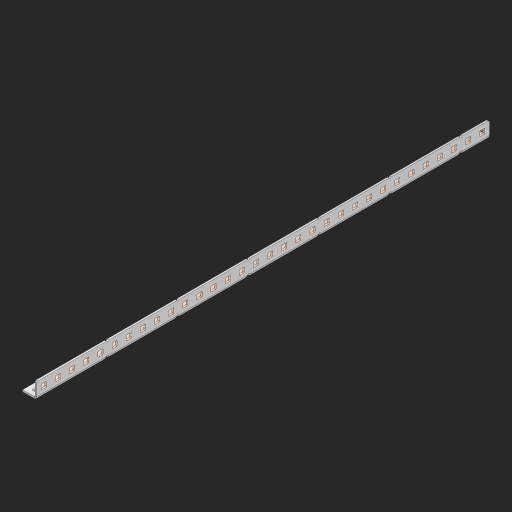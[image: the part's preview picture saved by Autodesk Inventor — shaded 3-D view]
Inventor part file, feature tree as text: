
AUTODESK INVENTOR PART (.ipt)
format: ipt  version: 2023 (Build 270158000, 158)  size: 1,003,520 bytes
history: native  units: in
note: dims shown in document units (in); Inventor stores cm internally (conversion verified against a paired STEP export)
features: other x69, extrude x63, sheet_metal_op x10, sketch x8, mirror x1, pattern_linear x1, chamfer x1
ambient origin geometry x8: Origin, YZ Plane, XZ Plane, XY Plane, X Axis, Y Axis, Z Axis, Center Point
bodies: Solid1 (feature_tree), Body (feature_tree)
feature tree (153):
  other  "Flange Pattern Plane"
  sheet_metal_op  "Flange Pattern"
  sheet_metal_op  "Body Pattern"
  other  "Arc Length"
  mirror  "Notch Mirror"
  pattern_linear  "Notch Pattern"  Spacing1=0.25in  [1 undecoded]
  chamfer  "End Chamfer"
  extrude  "Half Cut"  Depth=0.0625in
  sketch  "Sketch1"  dims[d0=1.5in]
  other  "Plate1"
  sketch  "Sketch2"  dims[d1=16.0in]
  other  "Plate2"
  sheet_metal_op  "Bend1"
  sheet_metal_op  "Corner1"
  sketch  "Sketch3"  dims[d2=0.0625in]
  other  "Flange Pattern Sketch"
  sketch  "Sketch7"  dims[d3=0.0625in]
  other  "Srf1"
  other  "Srf2"
  sketch  "Sketch8"  dims[d4=0.0312in]
  sketch  "Sketch9"  dims[d5=0.125in]
  other  "Srf91"
  sheet_metal_op  "Body Pattern Sketch"
  other  "Srf92"
  sketch  "Sketch13"  dims[d6=0.0625in]
  sketch  "Sketch14"  dims[d7=0.5in d8=90.0deg d9=0.0312in d10=0.25in d11=0.0625in d12=0.0625in d16=0.182in d17=0.02in d18=0.0625in d19=0.0in d20=0.25in d21=0.25in d46=0.172in d47=1.0in d48=0.0in d49=0.182in d50=0.02in d51=0.25in d52=0.25in d53=0.0625in d54=0.0in d55=0.172in d56=1.0in d57=0.0in d60=12.5984in d62=0.5in d63=0.3937in d65=0.5in d85=0.1473in d86=0.1782in d88=0.04in d89=0.0625in d90=0.0in d91=0.04in d92=0.0491in d95=2.5in d96=0.04in d97=0.25in d98=45.0deg d101=0.0in d102=2.497in d131=0.5in d132=12.5984in d134=0.5in d139=0.5in]
  other  "Srf856"
  other  "Srf1310"
  other  "Srf1311"
  other  "Srf1312"
  other  "Srf1376"
  other  "Srf1377"
  other  "Srf1728"
  other  "Srf1755"
  other  "Srf1878"
  other  "Srf1879"
  other  "Srf1880"
  other  "Srf1881"
  other  "Srf1882"
  other  "Srf1883"
  other  "Srf1884"
  other  "Srf1885"
  other  "Srf1886"
  other  "Srf1887"
  other  "Srf1888"
  other  "Srf1889"
  other  "Srf1890"
  other  "Srf1891"
  other  "Srf1892"
  other  "Srf1893"
  other  "Srf1894"
  other  "Srf1895"
  other  "Srf1896"
  other  "Srf1897"
  other  "Srf1898"
  other  "Srf1899"
  other  "Srf1900"
  other  "Srf1901"
  other  "Srf1902"
  other  "Srf1903"
  other  "Srf1942"
  other  "Srf1943"
  other  "Srf1944"
  other  "Srf1945"
  other  "Srf1946"
  other  "Srf1947"
  other  "Srf1948"
  other  "Srf1949"
  other  "Srf1950"
  other  "Srf1951"
  other  "Srf1952"
  other  "Srf1953"
  other  "Srf1954"
  other  "Srf1955"
  other  "Srf1956"
  other  "Srf1957"
  other  "Srf1958"
  other  "Srf1959"
  other  "Srf1960"
  other  "Srf1961"
  other  "Srf1962"
  other  "Srf1963"
  other  "Srf1964"
  other  "Srf1965"
  other  "Srf1966"
  other  "Srf1967"
  sheet_metal_op  "Flange Stamp"
  sheet_metal_op  "Flange Circle"
  sheet_metal_op  "Body Stamp"
  sheet_metal_op  "Body Circle"
  sheet_metal_op  "Notch"
  extrude  "ExtrusionSrf2"  Depth=0.0625in
  extrude  "ExtrusionSrf92"  Depth=0.5in
  extrude  "ExtrusionSrf856"  Depth=0.02in
  extrude  "ExtrusionSrf1310"  Depth=0.0625in
  extrude  "ExtrusionSrf1311"  TaperAngle=0.0deg  [1 undecoded]
  extrude  "ExtrusionSrf1312"  Depth=0.5in
  extrude  "ExtrusionSrf1376"  Depth=0.5in
  extrude  "ExtrusionSrf1377"  Depth=0.5in
  extrude  "ExtrusionSrf1728"  Depth=0.5in TaperAngle=0.0deg
  extrude  "ExtrusionSrf1755"  Depth=0.5in
  extrude  "ExtrusionSrf1878"  Depth=0.02in
  extrude  "ExtrusionSrf1879"  Depth=0.5in
  extrude  "ExtrusionSrf1880"  Depth=0.5in
  extrude  "ExtrusionSrf1881"  Depth=0.0625in
  extrude  "ExtrusionSrf1882"  TaperAngle=0.0deg  [1 undecoded]
  extrude  "ExtrusionSrf1883"  Depth=0.5in
  extrude  "ExtrusionSrf1884"  Depth=0.5in TaperAngle=0.0deg
  extrude  "ExtrusionSrf1885"  Depth=0.5in
  extrude  "ExtrusionSrf1886"  Depth=0.5in
  extrude  "ExtrusionSrf1887"  Depth=0.5in
  extrude  "ExtrusionSrf1888"  Depth=0.5in
  extrude  "ExtrusionSrf1889"  Depth=0.5in
  extrude  "ExtrusionSrf1890"  Depth=0.0625in
  extrude  "ExtrusionSrf1891"  TaperAngle=0.0deg  [1 undecoded]
  extrude  "ExtrusionSrf1892"  Depth=0.5in
  extrude  "ExtrusionSrf1893"  Depth=0.5in
  extrude  "ExtrusionSrf1894"  Depth=0.5in
  extrude  "ExtrusionSrf1895"  Depth=0.5in TaperAngle=45.0deg
  extrude  "ExtrusionSrf1896"  TaperAngle=0.0deg  [1 undecoded]
  extrude  "ExtrusionSrf1897"  Depth=0.5in
  extrude  "ExtrusionSrf1898"  Depth=0.5in
  extrude  "ExtrusionSrf1899"  Depth=0.5in
  extrude  "ExtrusionSrf1900"  Depth=0.5in
  extrude  "ExtrusionSrf1901"  Depth=0.5in
  extrude  "ExtrusionSrf1902"  [1 undecoded]
  extrude  "ExtrusionSrf1903"  [1 undecoded]
  extrude  "ExtrusionSrf1942"  [1 undecoded]
  extrude  "ExtrusionSrf1943"  [1 undecoded]
  extrude  "ExtrusionSrf1944"  [1 undecoded]
  extrude  "ExtrusionSrf1945"  [1 undecoded]
  extrude  "ExtrusionSrf1946"  [1 undecoded]
  extrude  "ExtrusionSrf1947"  [1 undecoded]
  extrude  "ExtrusionSrf1948"  [1 undecoded]
  extrude  "ExtrusionSrf1949"  [1 undecoded]
  extrude  "ExtrusionSrf1950"  [1 undecoded]
  extrude  "ExtrusionSrf1951"  [1 undecoded]
  extrude  "ExtrusionSrf1952"  [1 undecoded]
  extrude  "ExtrusionSrf1953"  [1 undecoded]
  extrude  "ExtrusionSrf1954"  [1 undecoded]
  extrude  "ExtrusionSrf1955"  [1 undecoded]
  extrude  "ExtrusionSrf1956"  [1 undecoded]
  extrude  "ExtrusionSrf1957"  [1 undecoded]
  extrude  "ExtrusionSrf1958"  [1 undecoded]
  extrude  "ExtrusionSrf1959"  [1 undecoded]
  extrude  "ExtrusionSrf1960"  [1 undecoded]
  extrude  "ExtrusionSrf1961"  [1 undecoded]
  extrude  "ExtrusionSrf1962"  [1 undecoded]
  extrude  "ExtrusionSrf1963"  [1 undecoded]
  extrude  "ExtrusionSrf1964"  [1 undecoded]
  extrude  "ExtrusionSrf1965"  [1 undecoded]
  extrude  "ExtrusionSrf1966"  [1 undecoded]
  extrude  "ExtrusionSrf1967"  [1 undecoded]
note: 33 required parameter values undecoded (feature->parameter linkage not recoverable at this tier; creation-order binding heuristic only, values carry confidence <= 0.55)
